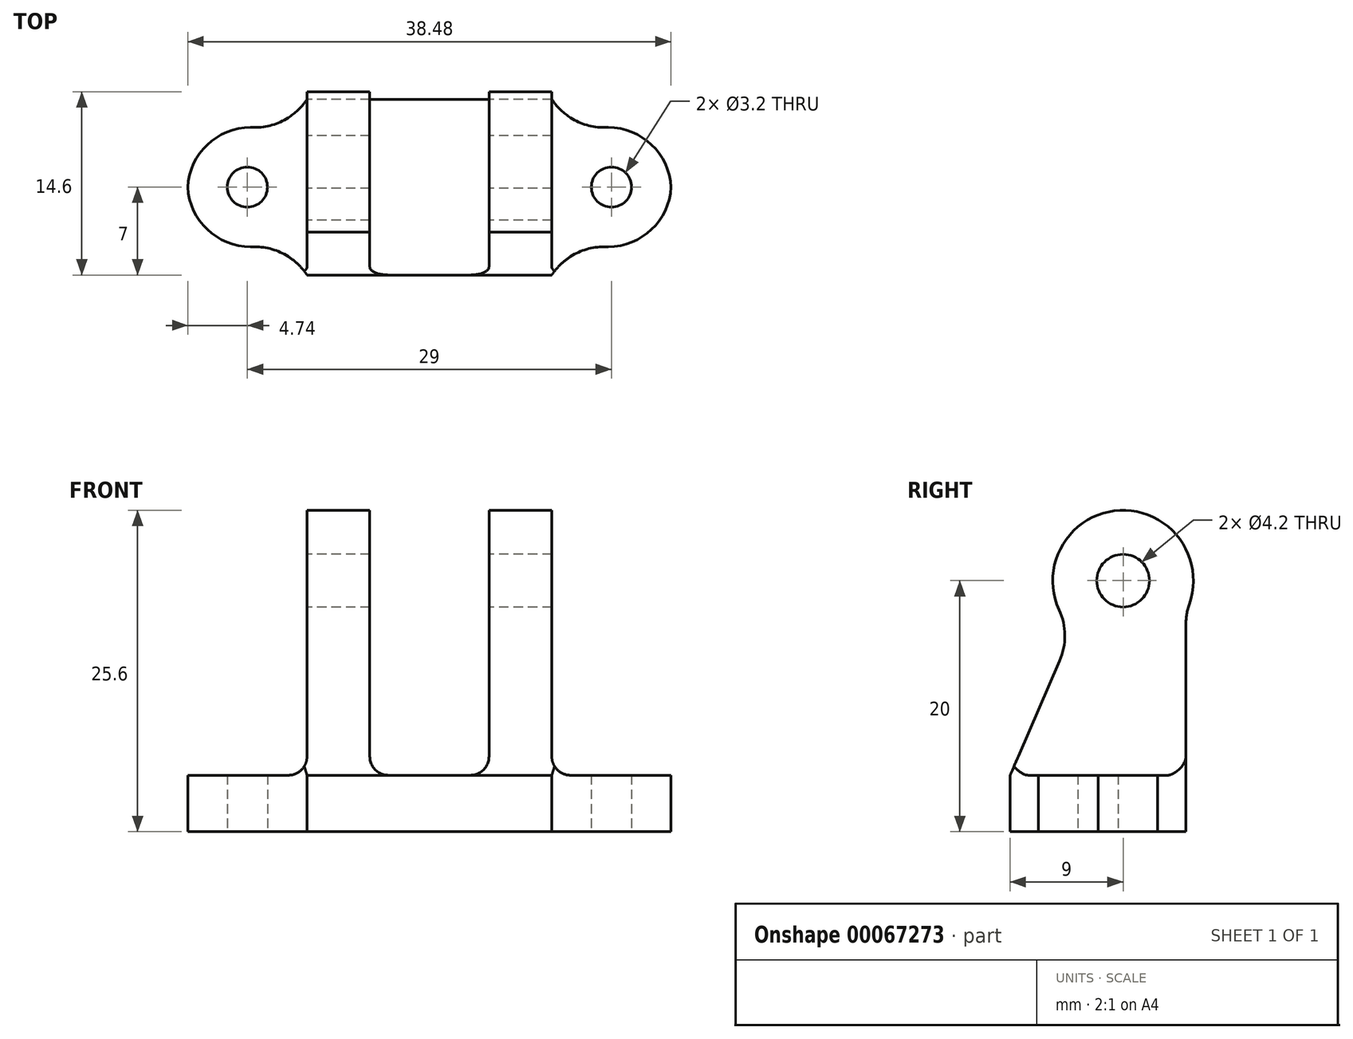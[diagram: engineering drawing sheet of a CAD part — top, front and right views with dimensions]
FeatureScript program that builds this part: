
annotation { "Feature Type Name" : "Feature", "Feature Type Description" : "" }
export const myFeature = defineFeature(function(context is Context, id is Id, definition is map)
    precondition{}
    {
        {
            var Q0;
            Q0=qCreatedBy(makeId("Top.planeOp"),FACE);
            var sketch = newSketch(context, id + "F0", { "sketchPlane" : qUnion([Q0])});
            skLineSegment(sketch, "E0.rect.right", {"start": v(9.75, 7) * mm, "end": v(9.75, -7) * mm});
            skPoint(sketch, "E0.rect.middle", {"position": v(0, 0) * mm});
            skLineSegment(sketch, "E1.left", {"start": v(-9.75, 7) * mm, "end": v(-9.75, -7) * mm});
            skLineSegment(sketch, "E2.left", {"start": v(9.75, 7) * mm, "end": v(9.75, -6.24) * mm});
            skLineSegment(sketch, "E2.right", {"start": v(19.25, 4.75) * mm, "end": v(19.25, -4.75) * mm});
            skLineSegment(sketch, "E3", {"start": v(-4.75, 7) * mm, "end": v(-4.75, -7) * mm});
            skLineSegment(sketch, "E4", {"start": v(4.75, 7) * mm, "end": v(4.75, -7) * mm});
            skLineSegment(sketch, "E5", {"start": v(-9.75, 7) * mm, "end": v(-4.75, 7) * mm});
            skLineSegment(sketch, "E6", {"start": v(4.75, 7) * mm, "end": v(9.75, 7) * mm});
            skLineSegment(sketch, "E7", {"start": v(4.75, 7) * mm, "end": v(-4.75, 7) * mm});
            skLineSegment(sketch, "E8", {"start": v(-9.75, -7) * mm, "end": v(-4.75, -7) * mm});
            skLineSegment(sketch, "E9", {"start": v(-4.75, -7) * mm, "end": v(4.75, -7) * mm});
            skLineSegment(sketch, "E10", {"start": v(4.75, -7) * mm, "end": v(9.75, -7) * mm});
            skLineSegment(sketch, "E11", {"start": v(-9.75, 4.75) * mm, "end": v(-19.25, 4.75) * mm});
            skLineSegment(sketch, "E12", {"start": v(19.25, -4.75) * mm, "end": v(9.75, -4.75) * mm});
            skLineSegment(sketch, "E13", {"start": v(19.25, 4.75) * mm, "end": v(9.75, 4.75) * mm});
            skLineSegment(sketch, "E14", {"start": v(-9.75, -4.75) * mm, "end": v(-19.25, -4.75) * mm});
            skLineSegment(sketch, "E15", {"start": v(0, 0) * mm, "end": v(-2.4, 0) * mm});
            skLineSegment(sketch, "E16", {"start": v(-19.25, 4.75) * mm, "end": v(-19.25, -4.75) * mm});
            skCircle(sketch, "E17", {"center": v(-14.5, 0) * mm, "radius": 1.6 * mm});
            skPoint(sketch, "E17.centerSnap0", {"position": v(-19.25, 0) * mm});
            skPoint(sketch, "E17.centerSnap1", {"position": v(-14.5, 4.75) * mm});
            skCircle(sketch, "E18", {"center": v(14.5, 0) * mm, "radius": 1.6 * mm});
            skPoint(sketch, "E18.centerSnap0", {"position": v(14.5, 4.75) * mm});
            skPoint(sketch, "E18.centerSnap1", {"position": v(-1.2, 0) * mm});
            skSolve(sketch);
        }
        {
            var Q0;
            {var subQ1=sQuery(id+"F0.wireOp",EDGE,"E11");Q0=makeQuery(id+"F0.imprint","IMPRINT",FACE,{"disambiguationData":[TD([[makeQuery(id+"F0.imprint","IMPRINT",EDGE,{"derivedFrom":subQ1}),1.0]])]});}
            var Q1;
            Q1=makeQuery(id+"F0.imprint","IMPRINT",FACE,{"disambiguationData":[TD([[makeQuery(id+"F0.imprint","IMPRINT",EDGE,{"derivedFrom":sQuery(id+"F0.wireOp",EDGE,"E3")}),-1.0]])]});
            var Q2;
            Q2=makeQuery(id+"F0.imprint","IMPRINT",FACE,{"disambiguationData":[TD([[makeQuery(id+"F0.imprint","IMPRINT",EDGE,{"derivedFrom":sQuery(id+"F0.wireOp",EDGE,"E3")}),1.0]])]});
            var Q3;
            {var subQ1=sQuery(id+"F0.wireOp",EDGE,"E0.rect.right");Q3=makeQuery(id+"F0.imprint","IMPRINT",FACE,{"disambiguationData":[TD([[makeQuery(id+"F0.imprint","IMPRINT",EDGE,{"derivedFrom":subQ1}),-1.0]])]});}
            var Q4;
            Q4=makeQuery(id+"F0.imprint","IMPRINT",FACE,{"disambiguationData":[TD([[makeQuery(id+"F0.imprint","IMPRINT",EDGE,{"derivedFrom":sQuery(id+"F0.wireOp",EDGE,"E2.right")}),-1.0]])]});
            extrude(context, id + "F1", {"entities" : qUnion([Q0, Q1, Q2, Q3, Q4]), "depth" : 4.5 * mm});
        }
        {
            var Q0;
            Q0=makeQuery(id+"F0.imprint","IMPRINT",FACE,{"disambiguationData":[TD([[makeQuery(id+"F0.imprint","IMPRINT",EDGE,{"derivedFrom":sQuery(id+"F0.wireOp",EDGE,"E3")}),-1.0]])]});
            var Q1;
            {var subQ1=sQuery(id+"F0.wireOp",EDGE,"E0.rect.right");Q1=makeQuery(id+"F0.imprint","IMPRINT",FACE,{"disambiguationData":[TD([[makeQuery(id+"F0.imprint","IMPRINT",EDGE,{"derivedFrom":subQ1}),-1.0]])]});}
            extrude(context, id + "F2", {"entities" : qUnion([Q0, Q1]), "operationType" : NewBodyOperationType.ADD, "depth" : 26 * mm});
        }
        {
            var Q0;
            {var subQ0=sQuery(id+"F0.wireOp",EDGE,"E1.left");Q0=makeQuery(id+"F2.boolean.opBoolean","MERGE",FACE,{"derivedFrom":[makeQuery(id+"F1.opExtrude","SWEPT_FACE",FACE,{"disambiguationData":[OSD([subQ0]),TDD([makeQuery(id+"F0.imprint","IMPRINT",EDGE,{"disambiguationData":[TD([[makeQuery(id+"F0.imprint","INTERSECT",VERTEX,{"derivedFrom":[subQ0,sQuery(id+"F0.wireOp",EDGE,"E5")]}),-1.0]])],"derivedFrom":subQ0})])]}),makeQuery(id+"F1.opExtrude","SWEPT_FACE",FACE,{"disambiguationData":[OSD([subQ0]),TDD([makeQuery(id+"F0.imprint","IMPRINT",EDGE,{"disambiguationData":[TD([[makeQuery(id+"F0.imprint","INTERSECT",VERTEX,{"derivedFrom":[subQ0,sQuery(id+"F0.wireOp",EDGE,"E8")]}),1.0]])],"derivedFrom":subQ0})])]}),makeQuery(id+"F2.opExtrude","SWEPT_FACE",FACE,{"disambiguationData":[OSD([subQ0])]})]});}
            var sketch = newSketch(context, id + "F3", { "sketchPlane" : qUnion([Q0])});
            skLineSegment(sketch, "E19.0", {"start": v(-7, 0) * mm, "end": v(7, 0) * mm});
            skCircle(sketch, "E20", {"center": v(-2, 20) * mm, "radius": 2.1 * mm});
            skArc(sketch, "E21.0", {"start": v(3.1, 17.67) * mm, "mid": v(-1.75, 25.6) * mm, "end": v(-7.28, 18.14) * mm});
            skPoint(sketch, "E22.0", {"position": v(7, 4.5) * mm});
            skLineSegment(sketch, "E23", {"start": v(7, 4.5) * mm, "end": v(3.05, 13.61) * mm});
            skPoint(sketch, "E24.orphan", {"position": v(0, 20.67) * mm});
            skLineSegment(sketch, "E25", {"start": v(-7, 0) * mm, "end": v(-7, 16.48) * mm});
            skPoint(sketch, "E26.visualSharp", {"position": v(1.99, 16.07) * mm});
            skArc(sketch, "E26.filletArc", {"start": v(3.1, 17.67) * mm, "mid": v(2.64, 15.65) * mm, "end": v(3.05, 13.61) * mm});
            skPoint(sketch, "E27.visualSharp", {"position": v(-7, 17.48) * mm});
            skArc(sketch, "E27.filletArc", {"start": v(-7, 16.48) * mm, "mid": v(-7.07, 17.33) * mm, "end": v(-7.28, 18.14) * mm});
            skSolve(sketch);
        }
        {
            var Q0;
            {var subQ3=sQuery(id+"F3.wireOp",EDGE,"E23");Q0=makeQuery(id+"F3.imprint","IMPRINT",FACE,{"disambiguationData":[TD([[makeQuery(id+"F3.imprint","IMPRINT",EDGE,{"derivedFrom":subQ3}),-1.0]])]});}
            var Q1;
            Q1=makeQuery(id+"F3.imprint","IMPRINT",FACE,{"disambiguationData":[TD([[makeQuery(id+"F3.imprint","IMPRINT",EDGE,{"derivedFrom":sQuery(id+"F3.wireOp",EDGE,"E20")}),1.0]])]});
            extrude(context, id + "F4", {"entities" : qUnion([Q0, Q1]), "operationType" : NewBodyOperationType.REMOVE, "oppositeDirection" : true, "depth" : 25 * mm});
        }
        {
            var Q0;
            {var subQ0=sQuery(id+"F3.wireOp",EDGE,"E27.filletArc");Q0=makeQuery(id+"F3.imprint","IMPRINT",FACE,{"disambiguationData":[TD([[makeQuery(id+"F3.imprint","IMPRINT",EDGE,{"derivedFrom":subQ0}),-1.0]])]});}
            var Q1;
            Q1=makeQuery(id+"F2.opExtrude","SWEPT_FACE",FACE,{"disambiguationData":[OSD([sQuery(id+"F0.wireOp",EDGE,"E3")])]});
            extrude(context, id + "F5", {"entities" : qUnion([Q0]), "operationType" : NewBodyOperationType.ADD, "endBound" : BoundingType.UP_TO_SURFACE, "oppositeDirection" : true, "endBoundEntityFace" : qUnion([Q1]), "depth" : 25 * mm});
        }
        {
            var Q0;
            {var subQ0=sQuery(id+"F3.wireOp",EDGE,"E27.filletArc");Q0=makeQuery(id+"F3.imprint","IMPRINT",FACE,{"disambiguationData":[TD([[makeQuery(id+"F3.imprint","IMPRINT",EDGE,{"derivedFrom":subQ0}),-1.0]])]});}
            var Q1;
            {var subQ0=sQuery(id+"F0.wireOp",EDGE,"E2.left");var subQ1=sQuery(id+"F0.wireOp",EDGE,"E0.rect.right");Q1=makeQuery(id+"F2.boolean.opBoolean","MERGE",FACE,{"derivedFrom":[makeQuery(id+"F1.opExtrude","SWEPT_FACE",FACE,{"disambiguationData":[OSD([subQ1,subQ0])]}),makeQuery(id+"F1.opExtrude","SWEPT_FACE",FACE,{"disambiguationData":[OSD([subQ0])]}),makeQuery(id+"F2.opExtrude","SWEPT_FACE",FACE,{"disambiguationData":[OSD([subQ1,subQ0])]})]});}
            var Q2;
            Q2=makeQuery(id+"F2.opExtrude","SWEPT_FACE",FACE,{"disambiguationData":[OSD([sQuery(id+"F0.wireOp",EDGE,"E4")])]});
            extrude(context, id + "F6", {"entities" : qUnion([Q0]), "operationType" : NewBodyOperationType.ADD, "endBound" : BoundingType.UP_TO_SURFACE, "oppositeDirection" : true, "endBoundEntityFace" : qUnion([Q1]), "depth" : 25 * mm, "hasSecondDirection" : true, "secondDirectionBound" : SecondDirectionBoundingType.UP_TO_SURFACE, "secondDirectionOppositeDirection" : true, "secondDirectionBoundEntityFace" : qUnion([Q2]), "secondDirectionDepth" : 25 * mm});
        }
        {
            var Q0;
            Q0=makeQuery(id+"F1.opExtrude","SWEPT_EDGE",EDGE,{"disambiguationData":[OSD([sQuery(id+"F0.wireOp",EDGE,"E2.left"),sQuery(id+"F0.wireOp",EDGE,"E12")])]});
            var Q1;
            Q1=makeQuery(id+"F1.opExtrude","SWEPT_EDGE",EDGE,{"disambiguationData":[OSD([sQuery(id+"F0.wireOp",EDGE,"E1.left"),sQuery(id+"F0.wireOp",EDGE,"E14")])]});
            var Q2;
            Q2=makeQuery(id+"F1.opExtrude","SWEPT_EDGE",EDGE,{"disambiguationData":[OSD([sQuery(id+"F0.wireOp",EDGE,"E14"),sQuery(id+"F0.wireOp",EDGE,"E16")])]});
            var Q3;
            Q3=makeQuery(id+"F1.opExtrude","SWEPT_EDGE",EDGE,{"disambiguationData":[OSD([sQuery(id+"F0.wireOp",EDGE,"E11"),sQuery(id+"F0.wireOp",EDGE,"E16")])]});
            var Q4;
            Q4=makeQuery(id+"F1.opExtrude","SWEPT_EDGE",EDGE,{"disambiguationData":[OSD([sQuery(id+"F0.wireOp",EDGE,"E1.left"),sQuery(id+"F0.wireOp",EDGE,"E11")])]});
            var Q5;
            Q5=makeQuery(id+"F1.opExtrude","SWEPT_EDGE",EDGE,{"disambiguationData":[OSD([sQuery(id+"F0.wireOp",EDGE,"E2.right"),sQuery(id+"F0.wireOp",EDGE,"E13")])]});
            var Q6;
            Q6=makeQuery(id+"F1.opExtrude","SWEPT_EDGE",EDGE,{"disambiguationData":[OSD([sQuery(id+"F0.wireOp",EDGE,"E2.right"),sQuery(id+"F0.wireOp",EDGE,"E12")])]});
            var Q7;
            Q7=makeQuery(id+"F1.opExtrude","SWEPT_EDGE",EDGE,{"disambiguationData":[OSD([sQuery(id+"F0.wireOp",EDGE,"E2.left"),sQuery(id+"F0.wireOp",EDGE,"E13")])]});
            fillet(context, id + "F7", {"entities" : qUnion([Q0, Q1, Q2, Q3, Q4, Q5, Q6, Q7]), "radius" : 5 * mm, "tangentPropagation" : true, "allowEdgeOverflow" : false});
        }
        {
            var Q0;
            Q0=makeQuery(id+"F2.boolean.opBoolean","INTERSECT",EDGE,{"derivedFrom":[makeQuery(id+"F1.opExtrude","CAP_FACE",FACE,{"disambiguationData":[OSD([sQuery(id+"F0.wireOp",EDGE,"E0.rect.right"),sQuery(id+"F0.wireOp",EDGE,"E1.left"),sQuery(id+"F0.wireOp",EDGE,"E2.left"),sQuery(id+"F0.wireOp",EDGE,"E2.right"),sQuery(id+"F0.wireOp",EDGE,"E5"),sQuery(id+"F0.wireOp",EDGE,"E6"),sQuery(id+"F0.wireOp",EDGE,"E7"),sQuery(id+"F0.wireOp",EDGE,"E8"),sQuery(id+"F0.wireOp",EDGE,"E9"),sQuery(id+"F0.wireOp",EDGE,"E10"),sQuery(id+"F0.wireOp",EDGE,"E11"),sQuery(id+"F0.wireOp",EDGE,"E12"),sQuery(id+"F0.wireOp",EDGE,"E13"),sQuery(id+"F0.wireOp",EDGE,"E14"),sQuery(id+"F0.wireOp",EDGE,"E16"),sQuery(id+"F0.wireOp",EDGE,"E17"),sQuery(id+"F0.wireOp",EDGE,"E18")])],"isStart":false}),makeQuery(id+"F2.opExtrude","SWEPT_FACE",FACE,{"disambiguationData":[OSD([sQuery(id+"F0.wireOp",EDGE,"E3")])]})]});
            var Q1;
            {var subQ0=sQuery(id+"F0.wireOp",EDGE,"E2.left");var subQ1=sQuery(id+"F0.wireOp",EDGE,"E0.rect.right");Q1=makeQuery(id+"F2.boolean.opBoolean","INTERSECT",EDGE,{"derivedFrom":[makeQuery(id+"F1.opExtrude","CAP_FACE",FACE,{"disambiguationData":[OSD([subQ1,sQuery(id+"F0.wireOp",EDGE,"E1.left"),subQ0,sQuery(id+"F0.wireOp",EDGE,"E2.right"),sQuery(id+"F0.wireOp",EDGE,"E5"),sQuery(id+"F0.wireOp",EDGE,"E6"),sQuery(id+"F0.wireOp",EDGE,"E7"),sQuery(id+"F0.wireOp",EDGE,"E8"),sQuery(id+"F0.wireOp",EDGE,"E9"),sQuery(id+"F0.wireOp",EDGE,"E10"),sQuery(id+"F0.wireOp",EDGE,"E11"),sQuery(id+"F0.wireOp",EDGE,"E12"),sQuery(id+"F0.wireOp",EDGE,"E13"),sQuery(id+"F0.wireOp",EDGE,"E14"),sQuery(id+"F0.wireOp",EDGE,"E16"),sQuery(id+"F0.wireOp",EDGE,"E17"),sQuery(id+"F0.wireOp",EDGE,"E18")])],"isStart":false}),makeQuery(id+"F2.opExtrude","SWEPT_FACE",FACE,{"disambiguationData":[OSD([subQ1,subQ0])]})]});}
            var Q2;
            Q2=makeQuery(id+"F2.boolean.opBoolean","INTERSECT",EDGE,{"derivedFrom":[makeQuery(id+"F1.opExtrude","CAP_FACE",FACE,{"disambiguationData":[OSD([sQuery(id+"F0.wireOp",EDGE,"E0.rect.right"),sQuery(id+"F0.wireOp",EDGE,"E1.left"),sQuery(id+"F0.wireOp",EDGE,"E2.left"),sQuery(id+"F0.wireOp",EDGE,"E2.right"),sQuery(id+"F0.wireOp",EDGE,"E5"),sQuery(id+"F0.wireOp",EDGE,"E6"),sQuery(id+"F0.wireOp",EDGE,"E7"),sQuery(id+"F0.wireOp",EDGE,"E8"),sQuery(id+"F0.wireOp",EDGE,"E9"),sQuery(id+"F0.wireOp",EDGE,"E10"),sQuery(id+"F0.wireOp",EDGE,"E11"),sQuery(id+"F0.wireOp",EDGE,"E12"),sQuery(id+"F0.wireOp",EDGE,"E13"),sQuery(id+"F0.wireOp",EDGE,"E14"),sQuery(id+"F0.wireOp",EDGE,"E16"),sQuery(id+"F0.wireOp",EDGE,"E17"),sQuery(id+"F0.wireOp",EDGE,"E18")])],"isStart":false}),makeQuery(id+"F2.opExtrude","SWEPT_FACE",FACE,{"disambiguationData":[OSD([sQuery(id+"F0.wireOp",EDGE,"E4")])]})]});
            var Q3;
            {var subQ0=sQuery(id+"F0.wireOp",EDGE,"E1.left");Q3=makeQuery(id+"F2.boolean.opBoolean","INTERSECT",EDGE,{"derivedFrom":[makeQuery(id+"F1.opExtrude","CAP_FACE",FACE,{"disambiguationData":[OSD([sQuery(id+"F0.wireOp",EDGE,"E0.rect.right"),subQ0,sQuery(id+"F0.wireOp",EDGE,"E2.left"),sQuery(id+"F0.wireOp",EDGE,"E2.right"),sQuery(id+"F0.wireOp",EDGE,"E5"),sQuery(id+"F0.wireOp",EDGE,"E6"),sQuery(id+"F0.wireOp",EDGE,"E7"),sQuery(id+"F0.wireOp",EDGE,"E8"),sQuery(id+"F0.wireOp",EDGE,"E9"),sQuery(id+"F0.wireOp",EDGE,"E10"),sQuery(id+"F0.wireOp",EDGE,"E11"),sQuery(id+"F0.wireOp",EDGE,"E12"),sQuery(id+"F0.wireOp",EDGE,"E13"),sQuery(id+"F0.wireOp",EDGE,"E14"),sQuery(id+"F0.wireOp",EDGE,"E16"),sQuery(id+"F0.wireOp",EDGE,"E17"),sQuery(id+"F0.wireOp",EDGE,"E18")])],"isStart":false}),makeQuery(id+"F2.opExtrude","SWEPT_FACE",FACE,{"disambiguationData":[OSD([subQ0])]})]});}
            fillet(context, id + "F8", {"entities" : qUnion([Q0, Q1, Q2, Q3]), "radius" : 1.5 * mm, "tangentPropagation" : true, "allowEdgeOverflow" : false});
        }
    });
